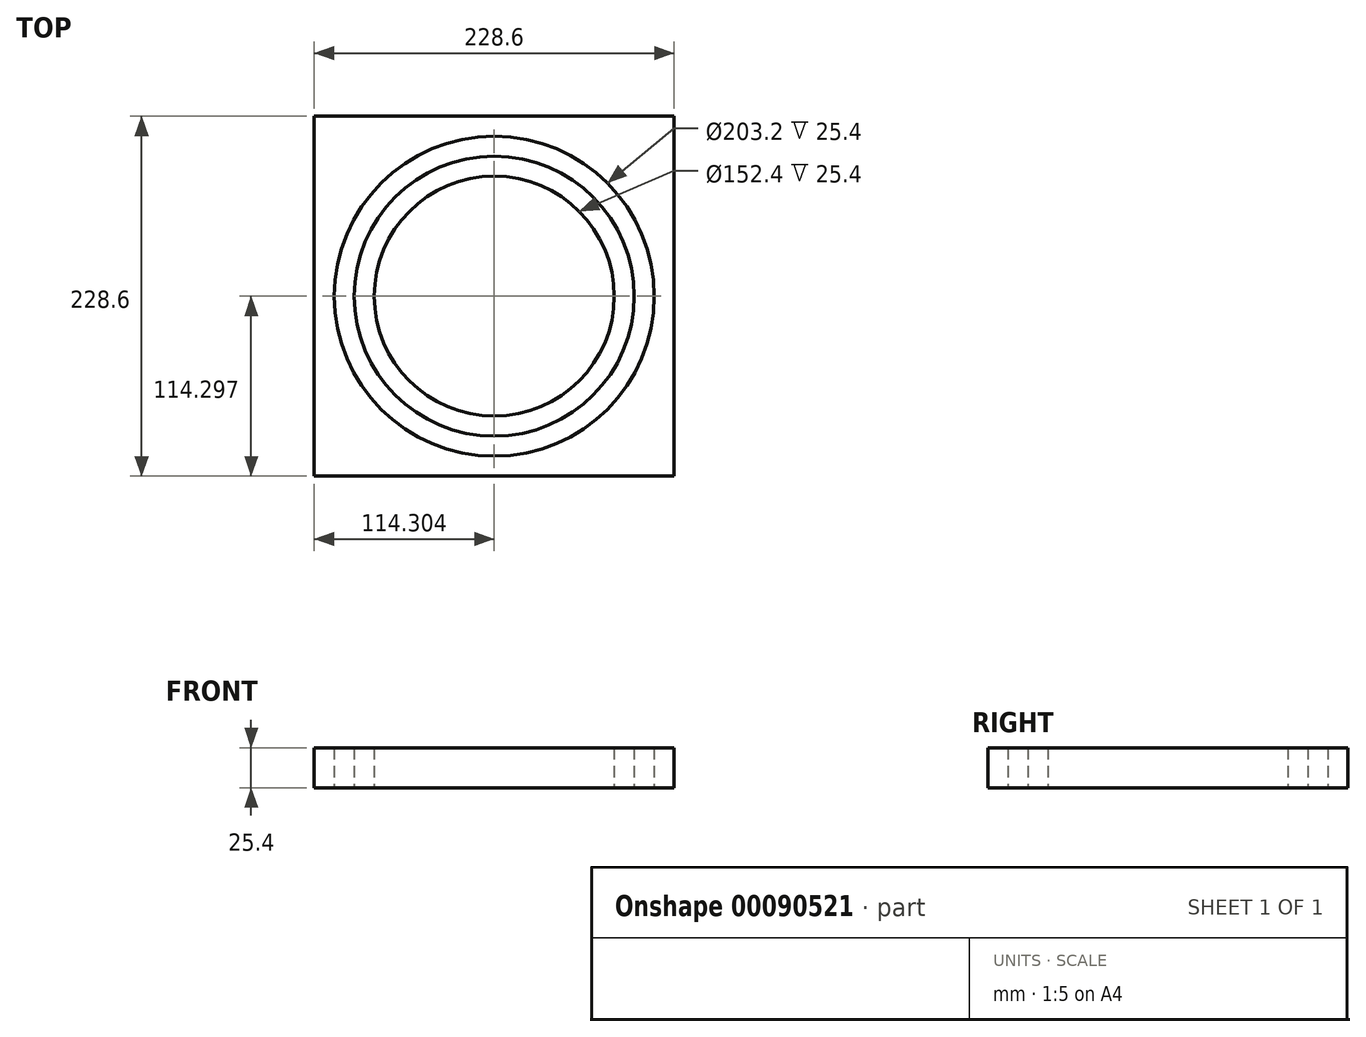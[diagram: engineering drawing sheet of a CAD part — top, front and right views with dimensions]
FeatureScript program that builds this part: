
annotation { "Feature Type Name" : "Feature", "Feature Type Description" : "" }
export const myFeature = defineFeature(function(context is Context, id is Id, definition is map)
    precondition{}
    {
        {
            var Q0;
            Q0=qCreatedBy(makeId("Top.planeOp"),FACE);
            var sketch = newSketch(context, id + "F0", { "sketchPlane" : qUnion([Q0])});
            skCircle(sketch, "E0", {"center": v(9.54, 52.35) * mm, "radius": 101.6 * mm});
            skLineSegment(sketch, "E1.bottom", {"start": v(123.84, -61.95) * mm, "end": v(-104.76, -61.95) * mm});
            skLineSegment(sketch, "E1.top", {"start": v(123.84, 166.65) * mm, "end": v(-104.76, 166.65) * mm});
            skLineSegment(sketch, "E1.left", {"start": v(123.84, -61.95) * mm, "end": v(123.84, 166.65) * mm});
            skLineSegment(sketch, "E1.right", {"start": v(-104.76, -61.95) * mm, "end": v(-104.76, 166.65) * mm});
            skCircle(sketch, "E2", {"center": v(9.54, 52.35) * mm, "radius": 76.2 * mm});
            skLineSegment(sketch, "E3", {"start": v(9.54, 52.35) * mm, "end": v(9.54, 128.55) * mm});
            skLineSegment(sketch, "E4", {"start": v(9.54, 52.35) * mm, "end": v(9.54, -23.85) * mm});
            skPoint(sketch, "E5", {"position": v(9.54, 14.25) * mm});
            skPoint(sketch, "E6", {"position": v(9.54, 90.45) * mm});
            skCircle(sketch, "E7", {"center": v(9.54, 52.35) * mm, "radius": 88.9 * mm});
            skSolve(sketch);
        }
        {
            var Q0;
            Q0=makeQuery(id+"F0.imprint","IMPRINT",FACE,{"disambiguationData":[TD([[makeQuery(id+"F0.imprint","IMPRINT",EDGE,{"derivedFrom":sQuery(id+"F0.wireOp",EDGE,"E0")}),-1.0]])]});
            var Q1;
            Q1=makeQuery(id+"F0.imprint","IMPRINT",FACE,{"disambiguationData":[TD([[makeQuery(id+"F0.imprint","IMPRINT",EDGE,{"derivedFrom":sQuery(id+"F0.wireOp",EDGE,"E7")}),1.0]])]});
            extrude(context, id + "F1", {"entities" : qUnion([Q0, Q1]), "depth" : 25.4 * mm});
        }
    });
